# Revit family: QF_BPRO_BT 800_566315
name_source: partatom
category: Sonderausstattung
revit_build: Autodesk Revit 2018 (Build: 20190510_1515(x64)
units: mm (PartAtom-declared; Revit-internal decimal feet)

## family parameters
Arbeitsebenenbasiert = Nein
Beim Laden mit Abzugskörper schneiden = Nein
Bemaßung runder Anschluss = Durchmesser verwenden
Gemeinsam genutzt = Nein
Immer vertikal = Ja
Raumberechnungspunkt = Ja
Teiletyp = Normal

## types (1)
- BT 800
    Artikel Nummer = 566315
    Beschreibung = Besteck- und Tablettwagen inkl. 10 Besteckbehälter
    Beschreibung durch Hersteller analog Leistungsverzeichniskurztext = Abmessungen

Länge:		900 mm
Breite:		600 mm  
Höhe:	   	1485 mm


Ausführung

Der Besteck- und Tablettwagen ist mit einem pultförmigen Besteckaufsatz inkl. 10 Besteckbehälter der Größe GN 1/4-150 aus CNS versehen. Beide Stirnseiten sind durch Kunststoff-Formschlußteile geschlossen. Das Fahrgestell ist aus stabilem 25 x 25 mm Vierkantrohr gebogen, dazwischen befindet sich ein Bord für die Tablettaufnahme. Das Bord ist eingeschweißt und hinten 50 mm aufgekantet (Durchschubsicherung).
Aus hygienischen Gründen sind alle Besteckbehälter mit transparenter, halbseitig klappbarer Plexiglasabdeckung ausgeführt. Der Behälterboden ist für ein gutes Greifen der Besteckteile entsprechend abgeschrägt. Speziell für Kuchengabeln und Kaffeelöffel ist der letzte Besteckbehälter mit Unterteilung. Im rechten Bereich direkt unter dem Aufsatz sind zwei Serviettenspender aus CNS für die Größe 125 x 90 mm montiert, diese sind von vorne beschickbar.

Der Besteck- und Tablettwagen ist fahrbar mittels stahlverzinkten Rollen (4  Lenkrollen, davon 2 mit Feststeller, Rollendurchmesser 125 mm). An allen vier Ecken befinden sich runde Wandabweiser.


Technische Daten

Werkstoff:   CNS 18/10
Gewicht:	   41 kg
Kapazität:   1100 Besteckteile;	120 Tabletts (Gastronorm oder 	Euronorm)

Besonderheit / Optionen

•	Zusätzlich sind zwei Servietten-Spender angebracht
•	Ausführung mit Gesamthöhe von 1120 mm für Kinder- / Schulverpflegung verfügbar

Fabrikat

Hersteller:   B.PRO
Modell:	     BT 800
Best.Nr.	     566315
    Beschreibung durch Hersteller analog Leistungsverzeichnislangtext = Abmessungen

Länge:		900 mm
Breite:		600 mm  
Höhe:	   	1485 mm


Ausführung

Der Besteck- und Tablettwagen ist mit einem pultförmigen Besteckaufsatz inkl. 10 Besteckbehälter der Größe GN 1/4-150 aus CNS versehen. Beide Stirnseiten sind durch Kunststoff-Formschlußteile geschlossen. Das Fahrgestell ist aus stabilem 25 x 25 mm Vierkantrohr gebogen, dazwischen befindet sich ein Bord für die Tablettaufnahme. Das Bord ist eingeschweißt und hinten 50 mm aufgekantet (Durchschubsicherung).
Aus hygienischen Gründen sind alle Besteckbehälter mit transparenter, halbseitig klappbarer Plexiglasabdeckung ausgeführt. Der Behälterboden ist für ein gutes Greifen der Besteckteile entsprechend abgeschrägt. Speziell für Kuchengabeln und Kaffeelöffel ist der letzte Besteckbehälter mit Unterteilung. Im rechten Bereich direkt unter dem Aufsatz sind zwei Serviettenspender aus CNS für die Größe 125 x 90 mm montiert, diese sind von vorne beschickbar.

Der Besteck- und Tablettwagen ist fahrbar mittels stahlverzinkten Rollen (4  Lenkrollen, davon 2 mit Feststeller, Rollendurchmesser 125 mm). An allen vier Ecken befinden sich runde Wandabweiser.


Technische Daten

Werkstoff:   CNS 18/10
Gewicht:	   41 kg
Kapazität:   1100 Besteckteile;	120 Tabletts (Gastronorm oder 	Euronorm)

Besonderheit / Optionen

•	Zusätzlich sind zwei Servietten-Spender angebracht
•	Ausführung mit Gesamthöhe von 1120 mm für Kinder- / Schulverpflegung verfügbar

Fabrikat

Hersteller:   B.PRO
Modell:	     BT 800
Best.Nr.	     566315
    CE Kennzeichnung = Ja
    Gerätegewicht Netto = 41.00 kg
    Großküchengerätezuordnung = Ja
    Hersteller = B.PRO GmbH
    Höhe = 1478 mm
    Internetadresse Gerätehersteller = https://www.bpro-solutions.com
    Internetadresse für Ersatzteilliste = https://www.bpro-solutions.com
    Kosten = 2398 $
    Länge Gerätebreite = 901 mm  [stored 2.95604 ft]
    Material = <Nach Kategorie>
    Modell = BT 800
    Sockelhöhe = 249 mm  [stored 0.816929 ft]
    Tiefe = 601 mm  [stored 1.97178 ft]
    Typenkommentare = Besteck- und Tablettwagen inkl. 10 Besteckbehälter
    URL = https://www.bpro-solutions.com
    Zubehör = Ja

note: [stored X ft] marks values corroborated as IEEE doubles in the binary element streams (Revit-internal decimal feet)
